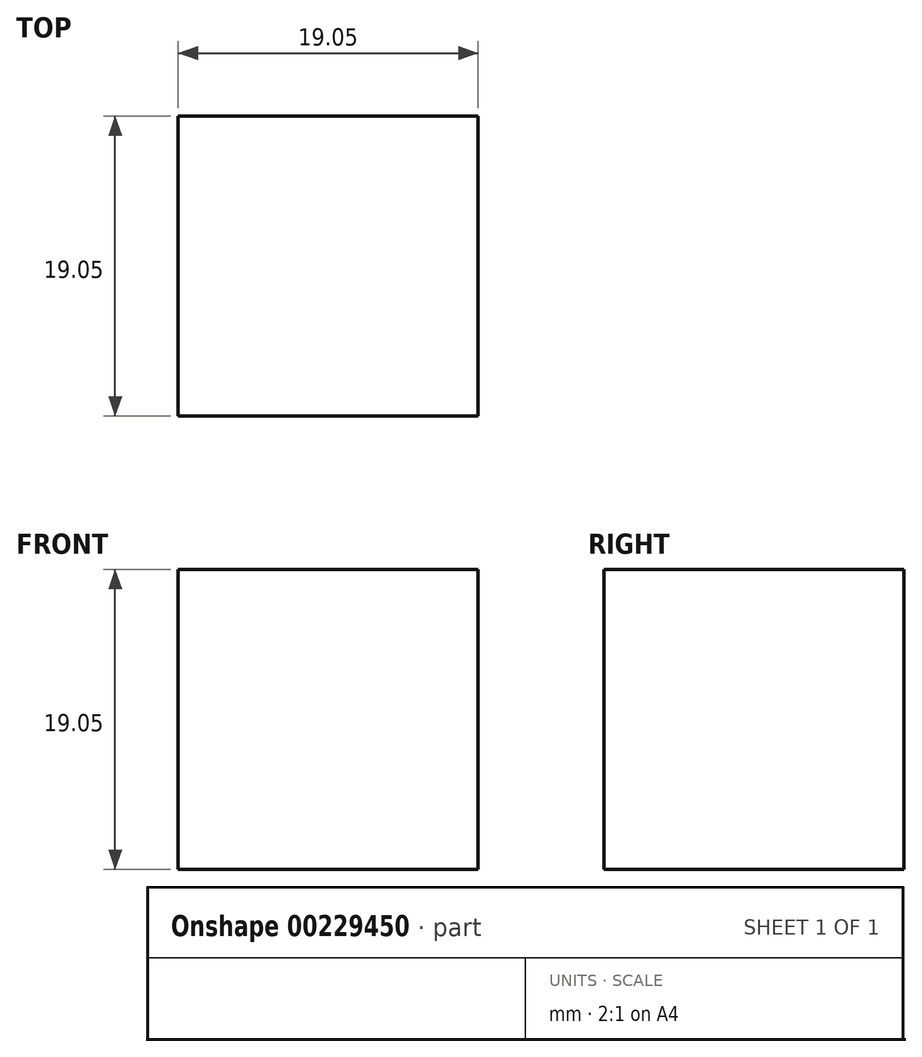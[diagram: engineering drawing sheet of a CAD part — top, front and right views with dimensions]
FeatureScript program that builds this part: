
annotation { "Feature Type Name" : "Feature", "Feature Type Description" : "" }
export const myFeature = defineFeature(function(context is Context, id is Id, definition is map)
    precondition{}
    {
        {
            var Q0;
            Q0=qCreatedBy(makeId("Top.planeOp"),FACE);
            var sketch = newSketch(context, id + "F0", { "sketchPlane" : qUnion([Q0])});
            skLineSegment(sketch, "E0.bottom", {"start": v(-11.16, -17.79) * mm, "end": v(7.9, -17.79) * mm});
            skLineSegment(sketch, "E0.top", {"start": v(-11.16, -36.84) * mm, "end": v(7.9, -36.84) * mm});
            skLineSegment(sketch, "E0.left", {"start": v(-11.16, -17.79) * mm, "end": v(-11.16, -36.84) * mm});
            skLineSegment(sketch, "E0.right", {"start": v(7.9, -17.79) * mm, "end": v(7.9, -36.84) * mm});
            skSolve(sketch);
        }
        {
            var Q0;
            Q0 = qSketchRegion(id + "F0", true);
            extrude(context, id + "F1", {"entities" : qUnion([Q0]), "depth" : 19.05 * mm});
        }
    });
